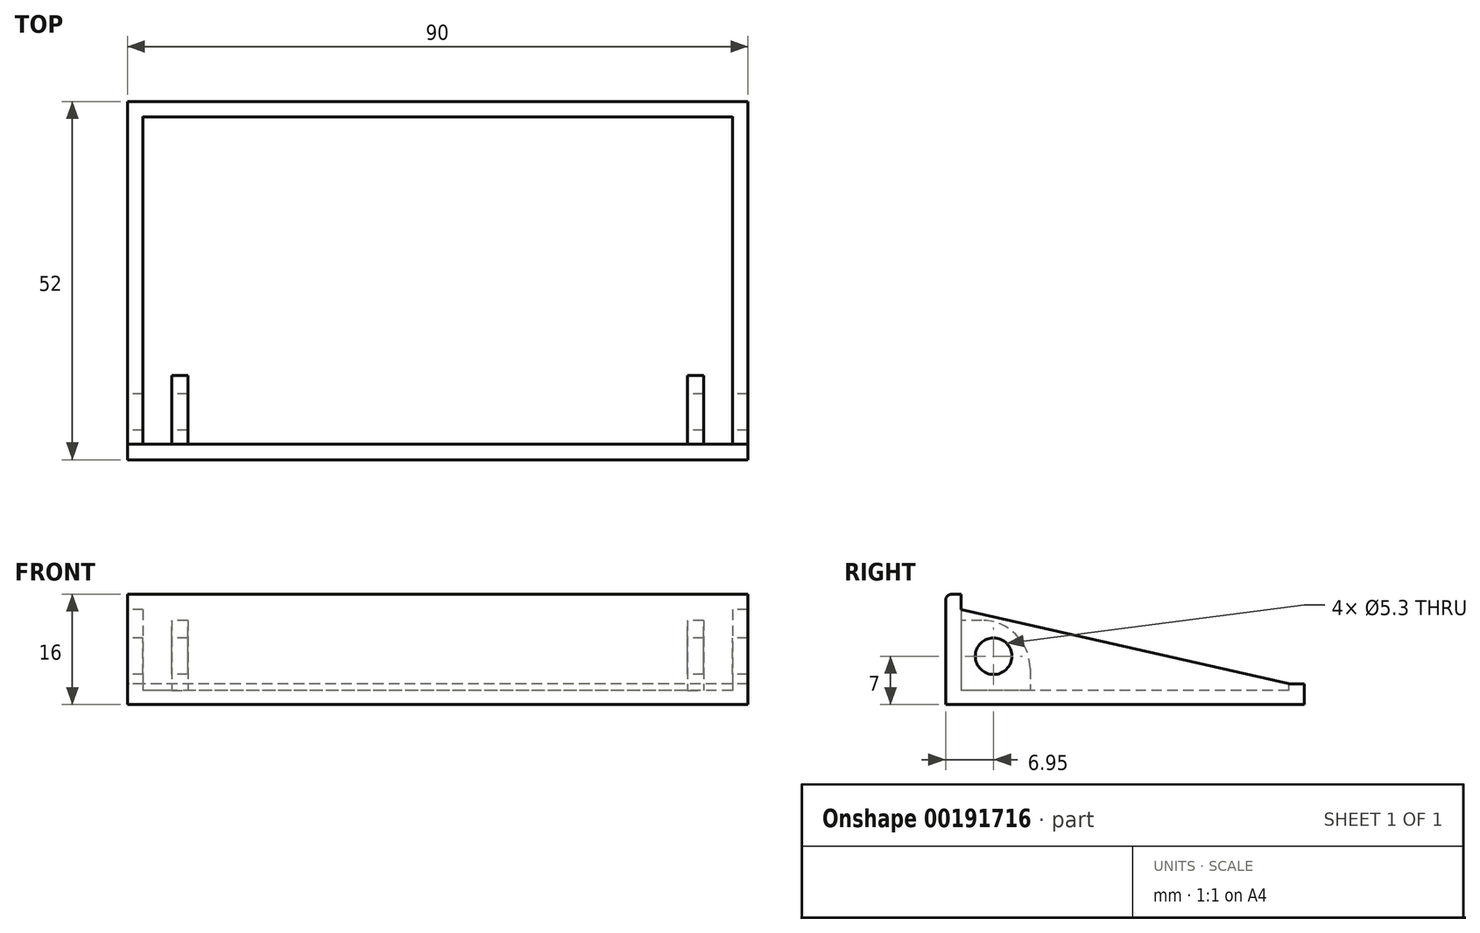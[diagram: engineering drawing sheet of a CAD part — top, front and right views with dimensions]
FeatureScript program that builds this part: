
annotation { "Feature Type Name" : "Feature", "Feature Type Description" : "" }
export const myFeature = defineFeature(function(context is Context, id is Id, definition is map)
    precondition{}
    {
        {
            var Q0;
            Q0=qCreatedBy(makeId("Top.planeOp"),FACE);
            var sketch = newSketch(context, id + "F0", { "sketchPlane" : qUnion([Q0])});
            skLineSegment(sketch, "E0.bottom", {"start": v(45, 26) * mm, "end": v(-45, 26) * mm});
            skLineSegment(sketch, "E0.top", {"start": v(45, -26) * mm, "end": v(-45, -26) * mm});
            skLineSegment(sketch, "E0.left", {"start": v(45, 26) * mm, "end": v(45, -26) * mm});
            skLineSegment(sketch, "E0.right", {"start": v(-45, 26) * mm, "end": v(-45, -26) * mm});
            skPoint(sketch, "E0.middle", {"position": v(0, 0) * mm});
            skLineSegment(sketch, "E1.bottom", {"start": v(42.75, 23.75) * mm, "end": v(-42.75, 23.75) * mm});
            skLineSegment(sketch, "E1.top", {"start": v(42.75, -23.75) * mm, "end": v(-42.75, -23.75) * mm});
            skLineSegment(sketch, "E1.left", {"start": v(42.75, 23.75) * mm, "end": v(42.75, -23.75) * mm});
            skLineSegment(sketch, "E1.right", {"start": v(-42.75, 23.75) * mm, "end": v(-42.75, -23.75) * mm});
            skLineSegment(sketch, "E2.bottom", {"start": v(-38.55, -13.75) * mm, "end": v(-36.25, -13.75) * mm});
            skLineSegment(sketch, "E2.top", {"start": v(-38.55, -23.75) * mm, "end": v(-36.25, -23.75) * mm});
            skLineSegment(sketch, "E2.left", {"start": v(-38.55, -13.75) * mm, "end": v(-38.55, -23.75) * mm});
            skLineSegment(sketch, "E2.right", {"start": v(-36.25, -13.75) * mm, "end": v(-36.25, -23.75) * mm});
            skLineSegment(sketch, "E3.bottom", {"start": v(36.25, -13.75) * mm, "end": v(38.55, -13.75) * mm});
            skLineSegment(sketch, "E3.top", {"start": v(36.25, -23.75) * mm, "end": v(38.55, -23.75) * mm});
            skLineSegment(sketch, "E3.left", {"start": v(36.25, -13.75) * mm, "end": v(36.25, -23.75) * mm});
            skLineSegment(sketch, "E3.right", {"start": v(38.55, -13.75) * mm, "end": v(38.55, -23.75) * mm});
            skSolve(sketch);
        }
        {
            var Q0;
            Q0 = qSketchRegion(id + "F0", true);
            extrude(context, id + "F1", {"entities" : qUnion([Q0]), "depth" : 16 * mm});
        }
        {
            var Q0;
            Q0=makeQuery(id+"F1.opExtrude","SWEPT_FACE",FACE,{"disambiguationData":[OSD([sQuery(id+"F0.wireOp",EDGE,"E0.right")])]});
            var sketch = newSketch(context, id + "F2", { "sketchPlane" : qUnion([Q0])});
            skLineSegment(sketch, "E4.bottom", {"start": v(-26, 0) * mm, "end": v(-23.75, 0) * mm});
            skLineSegment(sketch, "E4.top", {"start": v(-26, 3) * mm, "end": v(-23.75, 3) * mm});
            skLineSegment(sketch, "E4.left", {"start": v(-26, 0) * mm, "end": v(-26, 3) * mm});
            skLineSegment(sketch, "E4.right", {"start": v(-23.75, 0) * mm, "end": v(-23.75, 3) * mm});
            skLineSegment(sketch, "E5.bottom", {"start": v(26, 16) * mm, "end": v(23.75, 16) * mm});
            skLineSegment(sketch, "E5.top", {"start": v(26, 13.75) * mm, "end": v(23.75, 13.75) * mm});
            skLineSegment(sketch, "E5.left", {"start": v(26, 16) * mm, "end": v(26, 13.75) * mm});
            skLineSegment(sketch, "E5.right", {"start": v(23.75, 16) * mm, "end": v(23.75, 13.75) * mm});
            skLineSegment(sketch, "E6", {"start": v(-23.75, 3) * mm, "end": v(23.75, 13.75) * mm});
            skSolve(sketch);
        }
        {
            var Q0;
            {var subQ5=sQuery(id+"F2.wireOp",EDGE,"E4.top");Q0=makeQuery(id+"F2.imprint","IMPRINT",FACE,{"disambiguationData":[TD([[makeQuery(id+"F2.imprint","IMPRINT",EDGE,{"derivedFrom":subQ5}),1.0]])]});}
            extrude(context, id + "F3", {"entities" : qUnion([Q0]), "operationType" : NewBodyOperationType.REMOVE, "oppositeDirection" : true, "depth" : 1323 * mm});
        }
        {
            var Q0;
            Q0=makeQuery(id+"F0.imprint","IMPRINT",FACE,{"disambiguationData":[TD([[makeQuery(id+"F0.imprint","IMPRINT",EDGE,{"derivedFrom":sQuery(id+"F0.wireOp",EDGE,"E2.bottom")}),-1.0]])]});
            var Q1;
            Q1=makeQuery(id+"F0.imprint","IMPRINT",FACE,{"disambiguationData":[TD([[makeQuery(id+"F0.imprint","IMPRINT",EDGE,{"derivedFrom":sQuery(id+"F0.wireOp",EDGE,"E3.bottom")}),-1.0]])]});
            extrude(context, id + "F4", {"entities" : qUnion([Q0, Q1]), "operationType" : NewBodyOperationType.ADD, "depth" : 12.2 * mm});
        }
        {
            var Q0;
            Q0=makeQuery(id+"F4.opExtrude","SWEPT_FACE",FACE,{"disambiguationData":[OSD([sQuery(id+"F0.wireOp",EDGE,"E2.left")])]});
            var sketch = newSketch(context, id + "F5", { "sketchPlane" : qUnion([Q0])});
            skCircle(sketch, "E7", {"center": v(19.05, 7) * mm, "radius": 2.65 * mm});
            skPoint(sketch, "E7.centerSnap0", {"position": v(24.05, 7) * mm});
            skSolve(sketch);
        }
        {
            var Q0;
            Q0 = qSketchRegion(id + "F5", true);
            extrude(context, id + "F6", {"entities" : qUnion([Q0]), "operationType" : NewBodyOperationType.REMOVE, "oppositeDirection" : true, "depth" : 100 * mm, "hasSecondDirection" : true, "secondDirectionOppositeDirection" : false, "secondDirectionDepth" : 25 * mm});
        }
        {
            var Q0;
            Q0=makeQuery(id+"F0.imprint","IMPRINT",FACE,{"disambiguationData":[TD([[makeQuery(id+"F0.imprint","IMPRINT",EDGE,{"derivedFrom":sQuery(id+"F0.wireOp",EDGE,"E1.bottom")}),1.0]])]});
            var Q1;
            Q1=makeQuery(id+"F0.imprint","IMPRINT",FACE,{"disambiguationData":[TD([[makeQuery(id+"F0.imprint","IMPRINT",EDGE,{"derivedFrom":sQuery(id+"F0.wireOp",EDGE,"E0.bottom")}),1.0]])]});
            extrude(context, id + "F7", {"entities" : qUnion([Q0, Q1]), "operationType" : NewBodyOperationType.ADD, "depth" : 2 * mm});
        }
        {
            var Q0;
            Q0=makeQuery(id+"F4.opExtrude","CAP_EDGE",EDGE,{"disambiguationData":[OSD([sQuery(id+"F0.wireOp",EDGE,"E2.bottom")])],"isStart":false});
            var Q1;
            Q1=makeQuery(id+"F4.opExtrude","CAP_EDGE",EDGE,{"disambiguationData":[OSD([sQuery(id+"F0.wireOp",EDGE,"E3.bottom")])],"isStart":false});
            fillet(context, id + "F8", {"entities" : qUnion([Q0, Q1]), "radius" : 7 * mm, "tangentPropagation" : true, "allowEdgeOverflow" : false});
        }
        {
            var Q0;
            Q0=makeQuery(id+"F1.opExtrude","CAP_EDGE",EDGE,{"disambiguationData":[OSD([sQuery(id+"F0.wireOp",EDGE,"E0.top")])],"isStart":false});
            var Q1;
            Q1=makeQuery(id+"F3.boolean.opBoolean","MERGE",EDGE,{"derivedFrom":[makeQuery(id+"F1.opExtrude","CAP_EDGE",EDGE,{"disambiguationData":[OSD([sQuery(id+"F0.wireOp",EDGE,"E1.top"),sQuery(id+"F0.wireOp",EDGE,"E2.top"),sQuery(id+"F0.wireOp",EDGE,"E3.top")])],"isStart":false}),makeQuery(id+"F3.opExtrude","SWEPT_EDGE",EDGE,{"disambiguationData":[OSD([sQuery(id+"F0.wireOp",EDGE,"E0.right"),sQuery(id+"F2.wireOp",EDGE,"E5.bottom"),sQuery(id+"F2.wireOp",EDGE,"E5.right")])]})]});
            var Q2;
            {var subQ0=sQuery(id+"F2.wireOp",EDGE,"E4.top");Q2=makeQuery(id+"F3.boolean.opBoolean","COPY",EDGE,{"disambiguationData":[topologyDisambiguationEdgeConnected([makeQuery(id+"F1.opExtrude","SWEPT_FACE",FACE,{"disambiguationData":[OSD([sQuery(id+"F0.wireOp",EDGE,"E1.bottom")])]}),makeQuery(id+"F3.opExtrude","SWEPT_FACE",FACE,{"disambiguationData":[OSD([subQ0])]})])],"derivedFrom":makeQuery(id+"F3.opExtrude","SWEPT_EDGE",EDGE,{"disambiguationData":[OSD([subQ0,sQuery(id+"F2.wireOp",EDGE,"E4.right"),sQuery(id+"F2.wireOp",EDGE,"E6")])]})});}
            var Q3;
            Q3=makeQuery(id+"F3.boolean.opBoolean","COPY",EDGE,{"derivedFrom":makeQuery(id+"F3.opExtrude","SWEPT_EDGE",EDGE,{"disambiguationData":[OSD([sQuery(id+"F0.wireOp",EDGE,"E0.bottom"),sQuery(id+"F0.wireOp",EDGE,"E0.right"),sQuery(id+"F2.wireOp",EDGE,"E4.top"),sQuery(id+"F2.wireOp",EDGE,"E4.left")])]})});
            fillet(context, id + "F9", {"entities" : qUnion([Q0, Q1, Q2, Q3]), "radius" : 0.9 * mm, "tangentPropagation" : true, "allowEdgeOverflow" : false});
        }
    });
